# Revit family: MACK LED BOLLARD MBD-WB
name_source: partatom
category: Lighting Fixtures
units: mm (PartAtom-declared; Revit-internal decimal feet)

## family parameters
Cut with Voids When Loaded = No
Host = Face
Light Source = Yes
Part Type = Normal
Room Calculation Point = No
Round Connector Dimension = Use Diameter
Shared = No

## types (1)
- Mack Bollard
    Apparent Load = 0 VA
    Average life based on L70(HRS) = 100000
    Base Width = 3.54 "
    CRI = 80
    Color Filter = 16777215
    Default Elevation = 48 "
    Description = The MACK led bollard emphasizes a strong, ultra rectilinear design. It's fully shielded light source 
effectively contains upward light spill for safety and comfort of passers by. This bollard's overtly 
clean lines, with superior UV powder coating, quality die cast aluminum body, tempered safety glass
 lens, molded silicone gasket and stainless steel screws. This bollard is an excellent choice for 
walkways, entrances, promenades, plazas, courtyards, driveways, bridges, and landscaped areas.
    Dimming Lamp Color Temperature Shift = <None>
    Finish/Color = WOOD
    Fixture Height = 31.5 "
    Fixture Length = 5.12 "
    Fixture Width = 3.54 "
    LOWER PART FINISH = die cast aluminum
    Manufacturer = Above All Lighting
    Photometric Web File = generic
    Rod Length = 7.09 "
    TOP PART FINISH = die cast aluminum
    Tilt Angle = -90.00°
    Type Comments = MACK LED BOLLARD MBD-WB
    URL = https://www.abovealllighting.com
    Voltage = 277 V
    Voltage Comments = 120-277V
    Wattage Comments = 10W

## geometry (parser evidence)
native form markers: Sweep x3
no freeform markers — native parametric forms only
